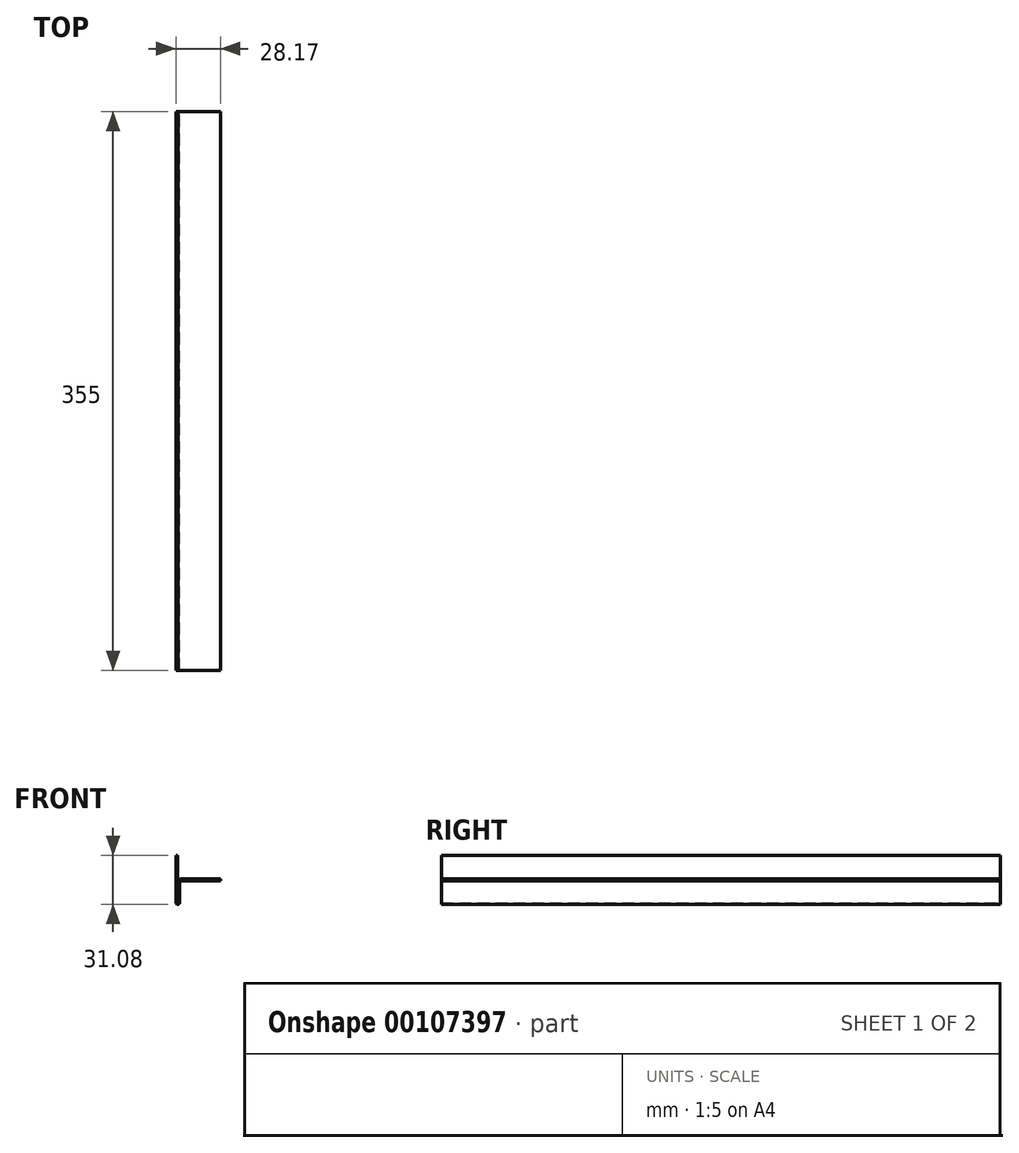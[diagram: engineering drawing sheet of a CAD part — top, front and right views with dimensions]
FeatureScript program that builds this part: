
annotation { "Feature Type Name" : "Feature", "Feature Type Description" : "" }
export const myFeature = defineFeature(function(context is Context, id is Id, definition is map)
    precondition{}
    {
        {
            var Q0;
            Q0=qCreatedBy(makeId("Front.planeOp"),FACE);
            var sketch = newSketch(context, id + "F0", { "sketchPlane" : qUnion([Q0])});
            skLineSegment(sketch, "E0", {"start": v(-5.17, 18) * mm, "end": v(-5.17, -12) * mm});
            skLineSegment(sketch, "E1", {"start": v(-5.17, 18) * mm, "end": v(-4.17, 18) * mm});
            skLineSegment(sketch, "E2", {"start": v(-4.17, 18) * mm, "end": v(-4.17, -12) * mm});
            skLineSegment(sketch, "E3", {"start": v(-4, -12) * mm, "end": v(-4, 1) * mm});
            skLineSegment(sketch, "E4", {"start": v(-2, 3) * mm, "end": v(23, 3) * mm});
            skPoint(sketch, "E5.visualSharp", {"position": v(-4, 3) * mm});
            skArc(sketch, "E5.filletArc", {"start": v(-2, 3) * mm, "mid": v(-3.41, 2.41) * mm, "end": v(-4, 1) * mm});
            skLineSegment(sketch, "E6.0", {"start": v(-2, 2) * mm, "end": v(23, 2) * mm});
            skArc(sketch, "E6.1", {"start": v(-2, 2) * mm, "mid": v(-2.7, 1.7) * mm, "end": v(-3, 1) * mm});
            skLineSegment(sketch, "E6.2", {"start": v(-3, -12) * mm, "end": v(-3, 1) * mm});
            skLineSegment(sketch, "E7", {"start": v(23, 3) * mm, "end": v(23, 2) * mm});
            skArc(sketch, "E8", {"start": v(-4, -12) * mm, "mid": v(-4.08, -12.08) * mm, "end": v(-4.17, -12) * mm});
            skArc(sketch, "E9", {"start": v(-5.17, -12) * mm, "mid": v(-4.08, -13.08) * mm, "end": v(-3, -12) * mm});
            skSolve(sketch);
        }
        {
            var Q0;
            Q0 = qSketchRegion(id + "F0", true);
            extrude(context, id + "F1", {"entities" : qUnion([Q0]), "depth" : 355 * mm});
        }
    });
